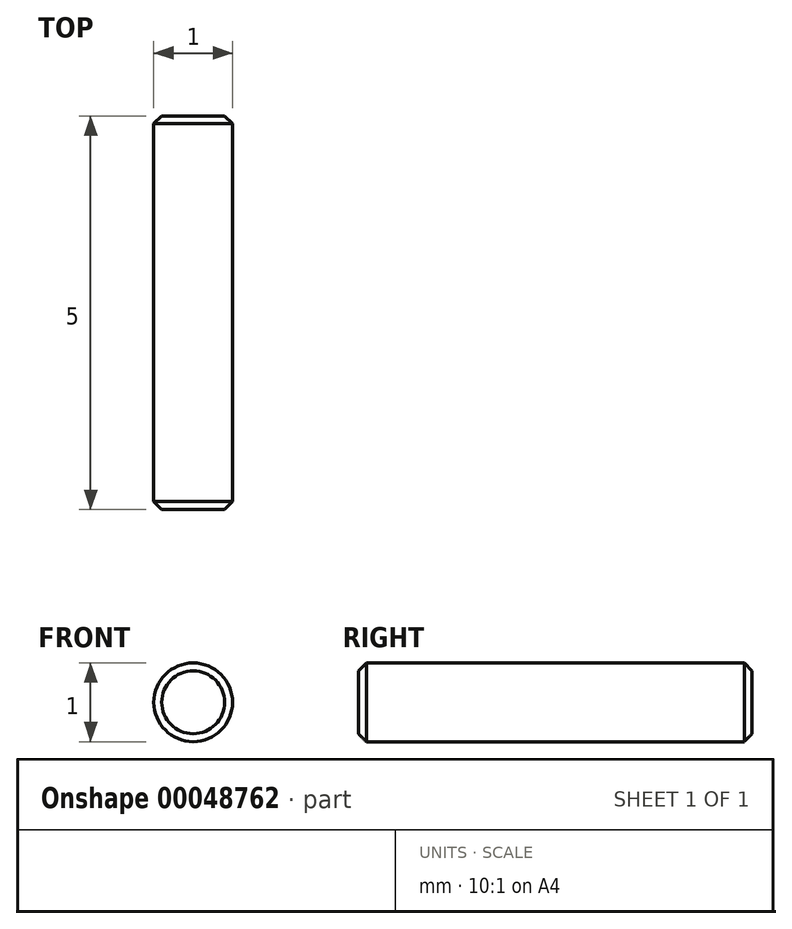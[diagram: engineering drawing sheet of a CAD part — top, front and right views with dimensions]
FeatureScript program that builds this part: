
annotation { "Feature Type Name" : "Feature", "Feature Type Description" : "" }
export const myFeature = defineFeature(function(context is Context, id is Id, definition is map)
    precondition{}
    {
        {
            var Q0;
            Q0=qCreatedBy(makeId("Front.planeOp"),FACE);
            var sketch = newSketch(context, id + "F0", { "sketchPlane" : qUnion([Q0])});
            skCircle(sketch, "E0", {"center": v(0, 0) * mm, "radius": 0.5 * mm});
            skSolve(sketch);
        }
        {
            var Q0;
            Q0=makeQuery(id+"F0.imprint","IMPRINT",FACE,{"disambiguationData":[TD([[makeQuery(id+"F0.imprint","IMPRINT",EDGE,{"derivedFrom":sQuery(id+"F0.wireOp",EDGE,"E0")}),1.0]])]});
            extrude(context, id + "F1", {"entities" : qUnion([Q0]), "offsetDistance" : 25 * mm, "depth" : 2.5 * mm});
        }
        {
            var Q0;
            Q0=makeQuery(id+"F1.opExtrude","CAP_EDGE",EDGE,{"disambiguationData":[OSD([sQuery(id+"F0.wireOp",EDGE,"E0")])],"isStart":false});
            chamfer(context, id + "F2", {"entities" : qUnion([Q0]), "width" : 0.1 * mm, "tangentPropagation" : true});
        }
        {
            var Q0;
            Q0=makeQuery(id+"F1.opExtrude","SWEPT_BODY",BODY,{"disambiguationData":[OSD([sQuery(id+"F0.wireOp",EDGE,"E0")])]});
            var Q1;
            Q1=qCreatedBy(makeId("Front.planeOp"),FACE);
            mirror(context, id + "F3", {"operationType" : NewBodyOperationType.ADD, "entities" : qUnion([Q0]), "mirrorPlane" : qUnion([Q1])});
        }
    });
